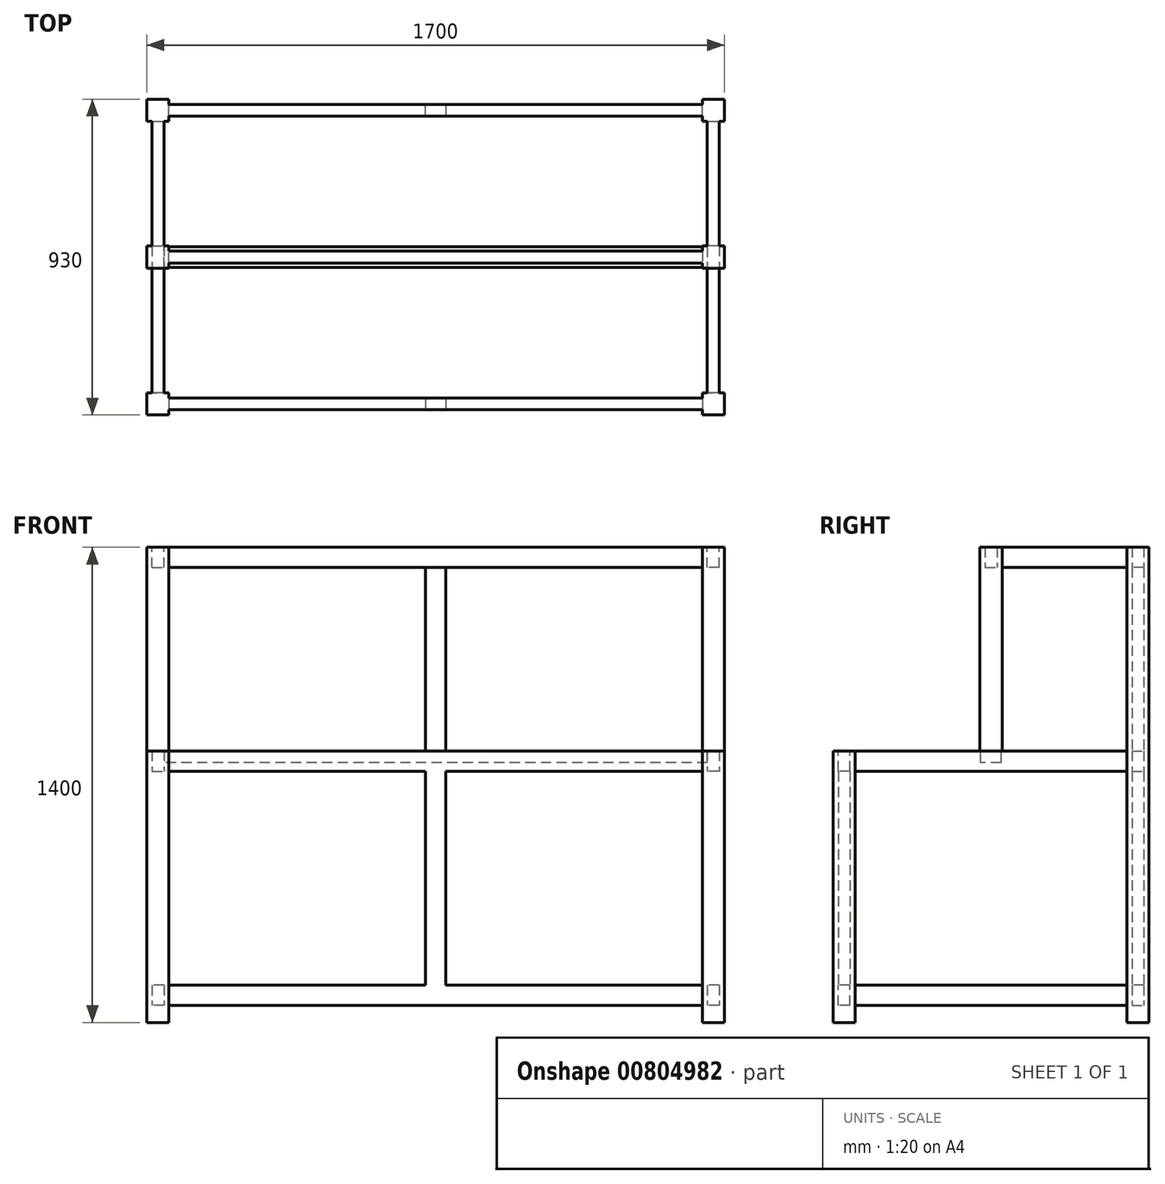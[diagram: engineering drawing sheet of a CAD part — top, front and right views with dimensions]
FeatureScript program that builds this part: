
annotation { "Feature Type Name" : "Feature", "Feature Type Description" : "" }
export const myFeature = defineFeature(function(context is Context, id is Id, definition is map)
    precondition{}
    {
        {
            var Q0;
            Q0=qCreatedBy(makeId("Front.planeOp"),FACE);
            var sketch = newSketch(context, id + "F0", { "sketchPlane" : qUnion([Q0])});
            skLineSegment(sketch, "E0.bottom", {"start": v(0, 0) * mm, "end": v(1700, 0) * mm});
            skLineSegment(sketch, "E0.top", {"start": v(0, 800) * mm, "end": v(1700, 800) * mm});
            skLineSegment(sketch, "E0.left", {"start": v(0, 0) * mm, "end": v(0, 800) * mm});
            skLineSegment(sketch, "E0.right", {"start": v(1700, 0) * mm, "end": v(1700, 800) * mm});
            skSolve(sketch);
        }
        {
            var Q0;
            Q0 = qSketchRegion(id + "F0", true);
            extrude(context, id + "F1", {"entities" : qUnion([Q0]), "depth" : 65 * mm, "offsetDistance" : 25 * mm});
        }
        {
            var Q0;
            Q0=makeQuery(id+"F1.opExtrude","SWEPT_FACE",FACE,{"disambiguationData":[OSD([sQuery(id+"F0.wireOp",EDGE,"E0.top")])]});
            var sketch = newSketch(context, id + "F2", { "sketchPlane" : qUnion([Q0])});
            skLineSegment(sketch, "E1.bottom", {"start": v(65, -65) * mm, "end": v(1635, -65) * mm});
            skLineSegment(sketch, "E1.top", {"start": v(65, -50) * mm, "end": v(1635, -50) * mm});
            skLineSegment(sketch, "E1.left", {"start": v(65, -65) * mm, "end": v(65, -50) * mm});
            skLineSegment(sketch, "E1.right", {"start": v(1635, -65) * mm, "end": v(1635, -50) * mm});
            skLineSegment(sketch, "E2.bottom", {"start": v(1635, 0) * mm, "end": v(65, 0) * mm});
            skLineSegment(sketch, "E2.top", {"start": v(1635, -15) * mm, "end": v(65, -15) * mm});
            skLineSegment(sketch, "E2.left", {"start": v(1635, 0) * mm, "end": v(1635, -15) * mm});
            skLineSegment(sketch, "E2.right", {"start": v(65, 0) * mm, "end": v(65, -15) * mm});
            skSolve(sketch);
        }
        {
            var Q0;
            Q0 = qSketchRegion(id + "F2", true);
            extrude(context, id + "F3", {"entities" : qUnion([Q0]), "operationType" : NewBodyOperationType.REMOVE, "endBound" : BoundingType.THROUGH_ALL, "oppositeDirection" : true, "depth" : 25 * mm, "offsetDistance" : 25 * mm});
        }
        {
            var Q0;
            Q0=makeQuery(id+"F3.boolean.opBoolean","COPY",FACE,{"derivedFrom":makeQuery(id+"F3.opExtrude","SWEPT_FACE",FACE,{"disambiguationData":[OSD([sQuery(id+"F2.wireOp",EDGE,"E1.top")])]})});
            var sketch = newSketch(context, id + "F4", { "sketchPlane" : qUnion([Q0])});
            skLineSegment(sketch, "E3.bottom", {"start": v(65, 0) * mm, "end": v(1635, 0) * mm});
            skLineSegment(sketch, "E3.top", {"start": v(65, 50) * mm, "end": v(1635, 50) * mm});
            skLineSegment(sketch, "E3.left", {"start": v(65, 0) * mm, "end": v(65, 50) * mm});
            skLineSegment(sketch, "E3.right", {"start": v(1635, 0) * mm, "end": v(1635, 50) * mm});
            skLineSegment(sketch, "E4.bottom", {"start": v(880, 740) * mm, "end": v(1635, 740) * mm});
            skLineSegment(sketch, "E4.top", {"start": v(880, 110) * mm, "end": v(1635, 110) * mm});
            skLineSegment(sketch, "E4.left", {"start": v(880, 740) * mm, "end": v(880, 110) * mm});
            skLineSegment(sketch, "E4.right", {"start": v(1635, 740) * mm, "end": v(1635, 110) * mm});
            skLineSegment(sketch, "E5.bottom", {"start": v(820, 110) * mm, "end": v(65, 110) * mm});
            skLineSegment(sketch, "E5.top", {"start": v(820, 740) * mm, "end": v(65, 740) * mm});
            skLineSegment(sketch, "E5.left", {"start": v(820, 110) * mm, "end": v(820, 740) * mm});
            skLineSegment(sketch, "E5.right", {"start": v(65, 110) * mm, "end": v(65, 740) * mm});
            skSolve(sketch);
        }
        {
            var Q0;
            Q0 = qSketchRegion(id + "F4", true);
            extrude(context, id + "F5", {"entities" : qUnion([Q0]), "operationType" : NewBodyOperationType.REMOVE, "endBound" : BoundingType.THROUGH_ALL, "oppositeDirection" : true, "depth" : 25 * mm, "offsetDistance" : 25 * mm});
        }
        {
            var Q0;
            {var subQ0=sQuery(id+"F0.wireOp",EDGE,"E0.bottom");var subQ1=sQuery(id+"F0.wireOp",EDGE,"E0.right");var subQ2=sQuery(id+"F0.wireOp",EDGE,"E0.top");Q0=makeQuery(id+"F3.boolean.opBoolean","SPLIT",FACE,{"disambiguationData":[TD([makeQuery(id+"F1.opExtrude","SWEPT_FACE",FACE,{"disambiguationData":[OSD([subQ1])]})])],"derivedFrom":makeQuery(id+"F1.opExtrude","CAP_FACE",FACE,{"disambiguationData":[OSD([subQ0,subQ2,sQuery(id+"F0.wireOp",EDGE,"E0.left"),subQ1])],"isStart":true})});}
            var sketch = newSketch(context, id + "F6", { "sketchPlane" : qUnion([Q0])});
            skLineSegment(sketch, "E6.bottom", {"start": v(-1685, 800) * mm, "end": v(-1650, 800) * mm});
            skLineSegment(sketch, "E6.top", {"start": v(-1685, 740) * mm, "end": v(-1650, 740) * mm});
            skLineSegment(sketch, "E6.left", {"start": v(-1685, 800) * mm, "end": v(-1685, 740) * mm});
            skLineSegment(sketch, "E6.right", {"start": v(-1650, 800) * mm, "end": v(-1650, 740) * mm});
            skLineSegment(sketch, "E7.bottom", {"start": v(-1685, 110) * mm, "end": v(-1650, 110) * mm});
            skLineSegment(sketch, "E7.top", {"start": v(-1685, 50) * mm, "end": v(-1650, 50) * mm});
            skLineSegment(sketch, "E7.left", {"start": v(-1685, 110) * mm, "end": v(-1685, 50) * mm});
            skLineSegment(sketch, "E7.right", {"start": v(-1650, 110) * mm, "end": v(-1650, 50) * mm});
            skLineSegment(sketch, "E8.bottom", {"start": v(-15, 800) * mm, "end": v(-50, 800) * mm});
            skLineSegment(sketch, "E8.top", {"start": v(-15, 740) * mm, "end": v(-50, 740) * mm});
            skLineSegment(sketch, "E8.left", {"start": v(-15, 800) * mm, "end": v(-15, 740) * mm});
            skLineSegment(sketch, "E8.right", {"start": v(-50, 800) * mm, "end": v(-50, 740) * mm});
            skLineSegment(sketch, "E9.bottom", {"start": v(-50, 110) * mm, "end": v(-15, 110) * mm});
            skLineSegment(sketch, "E9.top", {"start": v(-50, 50) * mm, "end": v(-15, 50) * mm});
            skLineSegment(sketch, "E9.left", {"start": v(-50, 110) * mm, "end": v(-50, 50) * mm});
            skLineSegment(sketch, "E9.right", {"start": v(-15, 110) * mm, "end": v(-15, 50) * mm});
            skSolve(sketch);
        }
        {
            var Q0;
            Q0 = qSketchRegion(id + "F6", true);
            extrude(context, id + "F7", {"entities" : qUnion([Q0]), "operationType" : NewBodyOperationType.ADD, "depth" : 800 * mm, "offsetDistance" : 25 * mm});
        }
        {
            var Q0;
            {var subQ0=sQuery(id+"F0.wireOp",EDGE,"E0.right");var subQ3=sQuery(id+"F0.wireOp",EDGE,"E0.bottom");Q0=makeQuery(id+"F5.boolean.opBoolean","SPLIT",FACE,{"disambiguationData":[TD([makeQuery(id+"F1.opExtrude","SWEPT_FACE",FACE,{"disambiguationData":[OSD([subQ0])]})])],"derivedFrom":makeQuery(id+"F1.opExtrude","SWEPT_FACE",FACE,{"disambiguationData":[OSD([subQ3])]})});}
            var sketch = newSketch(context, id + "F8", { "sketchPlane" : qUnion([Q0])});
            skLineSegment(sketch, "E10.bottom", {"start": v(1635, -800) * mm, "end": v(1700, -800) * mm});
            skLineSegment(sketch, "E10.top", {"start": v(1635, -865) * mm, "end": v(1700, -865) * mm});
            skLineSegment(sketch, "E10.left", {"start": v(1635, -800) * mm, "end": v(1635, -865) * mm});
            skLineSegment(sketch, "E10.right", {"start": v(1700, -800) * mm, "end": v(1700, -865) * mm});
            skLineSegment(sketch, "E11.bottom", {"start": v(0, -800) * mm, "end": v(65, -800) * mm});
            skLineSegment(sketch, "E11.top", {"start": v(0, -865) * mm, "end": v(65, -865) * mm});
            skLineSegment(sketch, "E11.left", {"start": v(0, -800) * mm, "end": v(0, -865) * mm});
            skLineSegment(sketch, "E11.right", {"start": v(65, -800) * mm, "end": v(65, -865) * mm});
            skSolve(sketch);
        }
        {
            var Q0;
            Q0 = qSketchRegion(id + "F8", true);
            extrude(context, id + "F9", {"entities" : qUnion([Q0]), "operationType" : NewBodyOperationType.ADD, "oppositeDirection" : true, "depth" : 1400 * mm, "offsetDistance" : 25 * mm});
        }
        {
            var Q0;
            Q0=makeQuery(id+"F9.opExtrude","SWEPT_FACE",FACE,{"disambiguationData":[OSD([sQuery(id+"F8.wireOp",EDGE,"E11.right")])]});
            var sketch = newSketch(context, id + "F10", { "sketchPlane" : qUnion([Q0])});
            skLineSegment(sketch, "E12.bottom", {"start": v(815, 1400) * mm, "end": v(850, 1400) * mm});
            skLineSegment(sketch, "E12.top", {"start": v(815, 1340) * mm, "end": v(850, 1340) * mm});
            skLineSegment(sketch, "E12.left", {"start": v(815, 1400) * mm, "end": v(815, 1340) * mm});
            skLineSegment(sketch, "E12.right", {"start": v(850, 1400) * mm, "end": v(850, 1340) * mm});
            skLineSegment(sketch, "E13.bottom", {"start": v(815, 110) * mm, "end": v(850, 110) * mm});
            skLineSegment(sketch, "E13.top", {"start": v(815, 50) * mm, "end": v(850, 50) * mm});
            skLineSegment(sketch, "E13.left", {"start": v(815, 110) * mm, "end": v(815, 50) * mm});
            skLineSegment(sketch, "E13.right", {"start": v(850, 110) * mm, "end": v(850, 50) * mm});
            skLineSegment(sketch, "E14.bottom", {"start": v(815, 800) * mm, "end": v(850, 800) * mm});
            skLineSegment(sketch, "E14.top", {"start": v(815, 740) * mm, "end": v(850, 740) * mm});
            skLineSegment(sketch, "E14.left", {"start": v(815, 800) * mm, "end": v(815, 740) * mm});
            skLineSegment(sketch, "E14.right", {"start": v(850, 800) * mm, "end": v(850, 740) * mm});
            skSolve(sketch);
        }
        {
            var Q0;
            Q0 = qSketchRegion(id + "F10", true);
            extrude(context, id + "F11", {"entities" : qUnion([Q0]), "operationType" : NewBodyOperationType.ADD, "depth" : 1570 * mm, "offsetDistance" : 25 * mm});
        }
        {
            var Q0;
            Q0=makeQuery(id+"F11.opExtrude","SWEPT_FACE",FACE,{"disambiguationData":[OSD([sQuery(id+"F10.wireOp",EDGE,"E13.bottom")])]});
            var sketch = newSketch(context, id + "F12", { "sketchPlane" : qUnion([Q0])});
            skLineSegment(sketch, "E15.bottom", {"start": v(820, 850) * mm, "end": v(880, 850) * mm});
            skLineSegment(sketch, "E15.top", {"start": v(820, 815) * mm, "end": v(880, 815) * mm});
            skLineSegment(sketch, "E15.left", {"start": v(880, 850) * mm, "end": v(880, 815) * mm});
            skLineSegment(sketch, "E15.right", {"start": v(820, 850) * mm, "end": v(820, 815) * mm});
            skSolve(sketch);
        }
        {
            var Q0;
            Q0 = qSketchRegion(id + "F12", true);
            var Q1;
            Q1=makeQuery(id+"F11.opExtrude","SWEPT_FACE",FACE,{"disambiguationData":[OSD([sQuery(id+"F10.wireOp",EDGE,"E12.top")])]});
            extrude(context, id + "F13", {"entities" : qUnion([Q0]), "operationType" : NewBodyOperationType.ADD, "endBound" : BoundingType.UP_TO_SURFACE, "depth" : 25 * mm, "endBoundEntityFace" : qUnion([Q1]), "offsetDistance" : 25 * mm});
        }
        {
            var Q0;
            Q0=makeQuery(id+"F7.opExtrude","SWEPT_FACE",FACE,{"disambiguationData":[OSD([sQuery(id+"F6.wireOp",EDGE,"E8.right")])]});
            var sketch = newSketch(context, id + "F14", { "sketchPlane" : qUnion([Q0])});
            skLineSegment(sketch, "E16.bottom", {"start": v(370, 800) * mm, "end": v(430, 800) * mm});
            skLineSegment(sketch, "E16.top", {"start": v(370, 765) * mm, "end": v(430, 765) * mm});
            skLineSegment(sketch, "E16.left", {"start": v(370, 800) * mm, "end": v(370, 765) * mm});
            skLineSegment(sketch, "E16.right", {"start": v(430, 800) * mm, "end": v(430, 765) * mm});
            skSolve(sketch);
        }
        {
            var Q0;
            Q0 = qSketchRegion(id + "F14", true);
            extrude(context, id + "F15", {"entities" : qUnion([Q0]), "operationType" : NewBodyOperationType.ADD, "endBound" : BoundingType.UP_TO_NEXT, "depth" : 25 * mm, "offsetDistance" : 25 * mm});
        }
        {
            var Q0;
            Q0=makeQuery(id+"F15.boolean.opBoolean","MERGE",FACE,{"derivedFrom":[makeQuery(id+"F7.boolean.opBoolean","MERGE",FACE,{"derivedFrom":[makeQuery(id+"F1.opExtrude","SWEPT_FACE",FACE,{"disambiguationData":[OSD([sQuery(id+"F0.wireOp",EDGE,"E0.top")])]}),makeQuery(id+"F7.opExtrude","SWEPT_FACE",FACE,{"disambiguationData":[OSD([sQuery(id+"F6.wireOp",EDGE,"E6.bottom")])]}),makeQuery(id+"F7.opExtrude","SWEPT_FACE",FACE,{"disambiguationData":[OSD([sQuery(id+"F6.wireOp",EDGE,"E8.bottom")])]})]}),makeQuery(id+"F15.opExtrude","SWEPT_FACE",FACE,{"disambiguationData":[OSD([sQuery(id+"F14.wireOp",EDGE,"E16.bottom")])]})]});
            var sketch = newSketch(context, id + "F16", { "sketchPlane" : qUnion([Q0])});
            skLineSegment(sketch, "E17.bottom", {"start": v(0, 432.5) * mm, "end": v(65, 432.5) * mm});
            skLineSegment(sketch, "E17.top", {"start": v(0, 367.5) * mm, "end": v(65, 367.5) * mm});
            skLineSegment(sketch, "E17.left", {"start": v(0, 432.5) * mm, "end": v(0, 367.5) * mm});
            skLineSegment(sketch, "E17.right", {"start": v(65, 432.5) * mm, "end": v(65, 367.5) * mm});
            skLineSegment(sketch, "E18.bottom", {"start": v(1635, 432.5) * mm, "end": v(1700, 432.5) * mm});
            skLineSegment(sketch, "E18.top", {"start": v(1635, 367.5) * mm, "end": v(1700, 367.5) * mm});
            skLineSegment(sketch, "E18.left", {"start": v(1635, 432.5) * mm, "end": v(1635, 367.5) * mm});
            skLineSegment(sketch, "E18.right", {"start": v(1700, 432.5) * mm, "end": v(1700, 367.5) * mm});
            skSolve(sketch);
        }
        {
            var Q0;
            Q0 = qSketchRegion(id + "F16", true);
            extrude(context, id + "F17", {"entities" : qUnion([Q0]), "operationType" : NewBodyOperationType.ADD, "depth" : 600 * mm, "offsetDistance" : 25 * mm});
        }
        {
            var Q0;
            Q0=makeQuery(id+"F9.opExtrude","SWEPT_FACE",FACE,{"disambiguationData":[OSD([sQuery(id+"F8.wireOp",EDGE,"E10.bottom")])]});
            var sketch = newSketch(context, id + "F18", { "sketchPlane" : qUnion([Q0])});
            skLineSegment(sketch, "E19.bottom", {"start": v(1650, 1400) * mm, "end": v(1685, 1400) * mm});
            skLineSegment(sketch, "E19.top", {"start": v(1650, 1340) * mm, "end": v(1685, 1340) * mm});
            skLineSegment(sketch, "E19.left", {"start": v(1650, 1400) * mm, "end": v(1650, 1340) * mm});
            skLineSegment(sketch, "E19.right", {"start": v(1685, 1400) * mm, "end": v(1685, 1340) * mm});
            skLineSegment(sketch, "E20.bottom", {"start": v(50, 1400) * mm, "end": v(15, 1400) * mm});
            skLineSegment(sketch, "E20.top", {"start": v(50, 1340) * mm, "end": v(15, 1340) * mm});
            skLineSegment(sketch, "E20.left", {"start": v(50, 1400) * mm, "end": v(50, 1340) * mm});
            skLineSegment(sketch, "E20.right", {"start": v(15, 1400) * mm, "end": v(15, 1340) * mm});
            skSolve(sketch);
        }
        {
            var Q0;
            Q0 = qSketchRegion(id + "F18", true);
            extrude(context, id + "F19", {"entities" : qUnion([Q0]), "operationType" : NewBodyOperationType.ADD, "endBound" : BoundingType.UP_TO_NEXT, "depth" : 25 * mm, "offsetDistance" : 25 * mm});
        }
        {
            var Q0;
            Q0=makeQuery(id+"F17.opExtrude","SWEPT_FACE",FACE,{"disambiguationData":[OSD([sQuery(id+"F16.wireOp",EDGE,"E17.right")])]});
            var sketch = newSketch(context, id + "F20", { "sketchPlane" : qUnion([Q0])});
            skLineSegment(sketch, "E21.bottom", {"start": v(382.5, 1400) * mm, "end": v(417.5, 1400) * mm});
            skLineSegment(sketch, "E21.top", {"start": v(382.5, 1340) * mm, "end": v(417.5, 1340) * mm});
            skLineSegment(sketch, "E21.left", {"start": v(382.5, 1400) * mm, "end": v(382.5, 1340) * mm});
            skLineSegment(sketch, "E21.right", {"start": v(417.5, 1400) * mm, "end": v(417.5, 1340) * mm});
            skSolve(sketch);
        }
        {
            var Q0;
            Q0 = qSketchRegion(id + "F20", true);
            extrude(context, id + "F21", {"entities" : qUnion([Q0]), "operationType" : NewBodyOperationType.ADD, "endBound" : BoundingType.UP_TO_NEXT, "depth" : 25 * mm, "offsetDistance" : 25 * mm});
        }
    });
